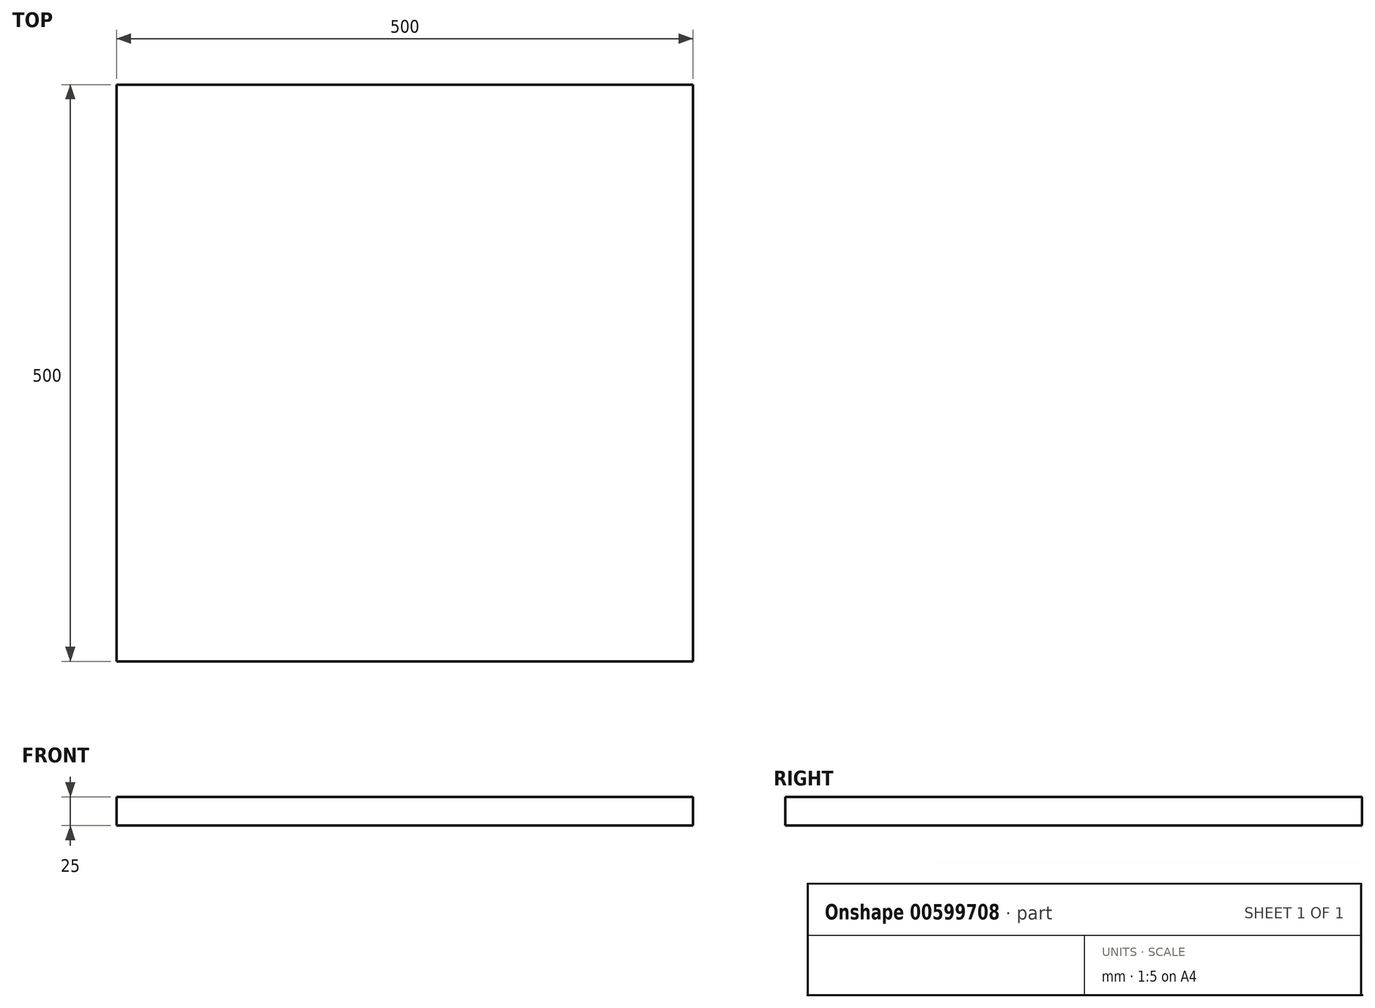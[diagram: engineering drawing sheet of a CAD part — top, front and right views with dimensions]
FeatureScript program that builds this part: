
annotation { "Feature Type Name" : "Feature", "Feature Type Description" : "" }
export const myFeature = defineFeature(function(context is Context, id is Id, definition is map)
    precondition{}
    {
        {
            var Q0;
            Q0=qCreatedBy(makeId("Top.planeOp"),FACE);
            var sketch = newSketch(context, id + "F0", { "sketchPlane" : qUnion([Q0])});
            skLineSegment(sketch, "E0.bottom", {"start": v(-250, 250) * mm, "end": v(250, 250) * mm});
            skLineSegment(sketch, "E0.top", {"start": v(-250, -250) * mm, "end": v(250, -250) * mm});
            skLineSegment(sketch, "E0.left", {"start": v(-250, 250) * mm, "end": v(-250, -250) * mm});
            skLineSegment(sketch, "E0.right", {"start": v(250, 250) * mm, "end": v(250, -250) * mm});
            skLineSegment(sketch, "E1", {"start": v(0, 250) * mm, "end": v(0, -250) * mm, "construction": true});
            skLineSegment(sketch, "E2", {"start": v(-250, 0) * mm, "end": v(250, 0) * mm, "construction": true});
            skSolve(sketch);
        }
        {
            var Q0;
            Q0=makeQuery(id+"F0.imprint","IMPRINT",FACE,{"disambiguationData":[TD([[makeQuery(id+"F0.imprint","IMPRINT",EDGE,{"derivedFrom":sQuery(id+"F0.wireOp",EDGE,"E0.bottom")}),-1.0]])]});
            extrude(context, id + "F1", {"entities" : qUnion([Q0]), "depth" : 25 * mm, "offsetDistance" : 25 * mm});
        }
    });
